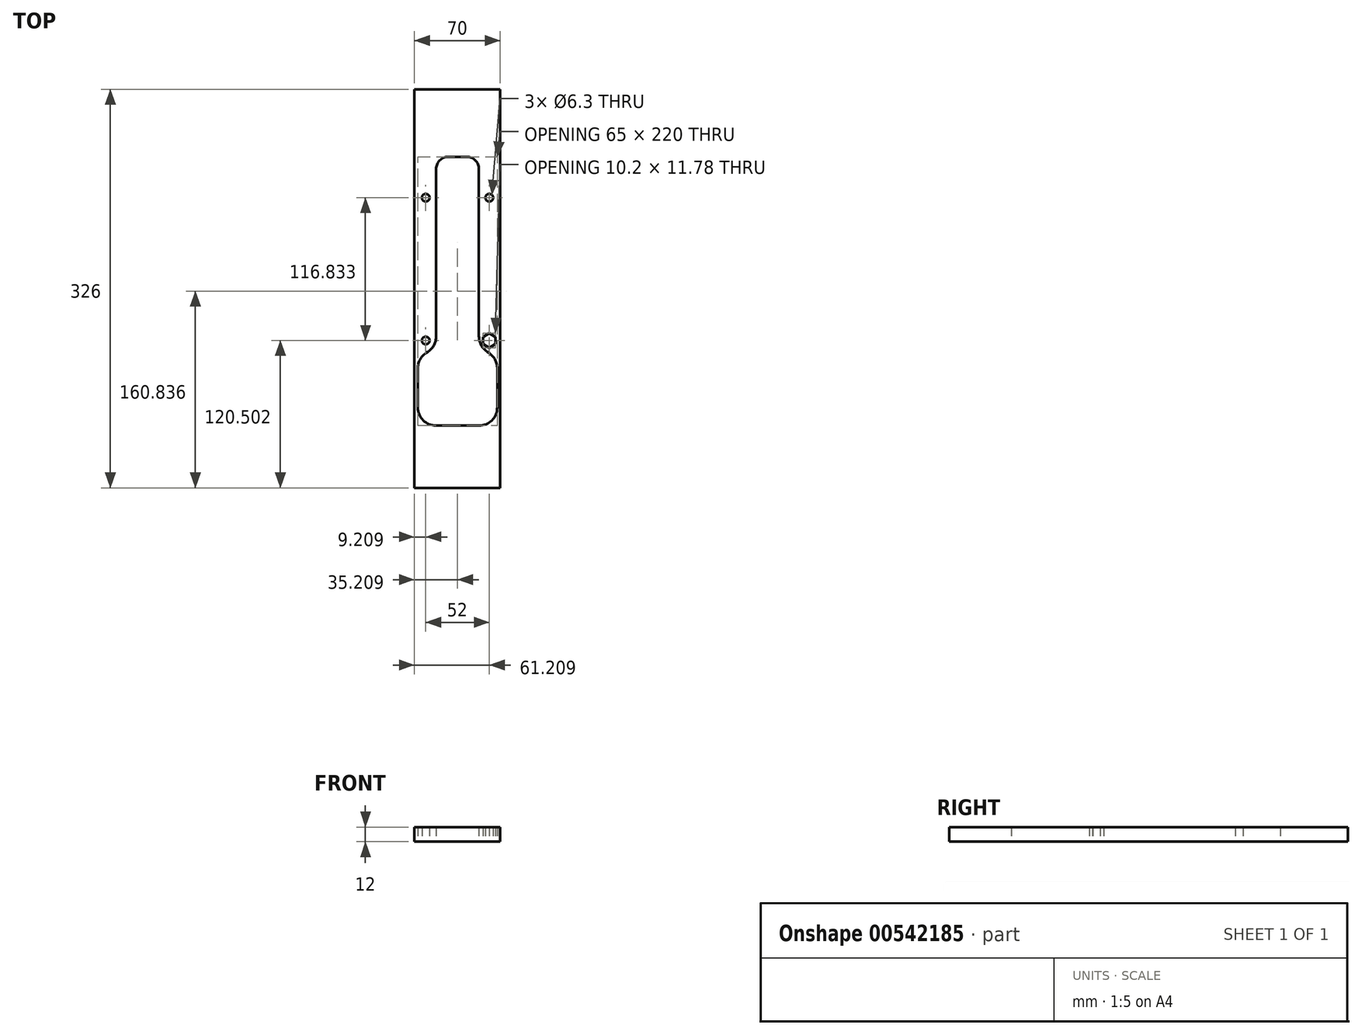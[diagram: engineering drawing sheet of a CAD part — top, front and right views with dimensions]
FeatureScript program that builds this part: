
annotation { "Feature Type Name" : "Feature", "Feature Type Description" : "" }
export const myFeature = defineFeature(function(context is Context, id is Id, definition is map)
    precondition{}
    {
        {
            var Q0;
            Q0=qCreatedBy(makeId("Top.planeOp"),FACE);
            var sketch = newSketch(context, id + "F0", { "sketchPlane" : qUnion([Q0])});
            skLineSegment(sketch, "E0.bottom", {"start": v(17.7, -112.16) * mm, "end": v(-17.3, -112.16) * mm});
            skLineSegment(sketch, "E0.top", {"start": v(17.7, 107.84) * mm, "end": v(-17.3, 107.84) * mm});
            skLineSegment(sketch, "E0.left", {"start": v(17.7, -47.16) * mm, "end": v(17.7, 107.84) * mm});
            skLineSegment(sketch, "E0.right", {"start": v(-17.3, -47.16) * mm, "end": v(-17.3, 107.84) * mm});
            skPoint(sketch, "E0.middle", {"position": v(0.2, -2.16) * mm});
            skLineSegment(sketch, "E1.bottom", {"start": v(32.7, -112.16) * mm, "end": v(-32.3, -112.16) * mm});
            skLineSegment(sketch, "E1.left", {"start": v(32.7, -112.16) * mm, "end": v(32.7, -57.16) * mm});
            skLineSegment(sketch, "E1.right", {"start": v(-32.3, -112.16) * mm, "end": v(-32.3, -57.16) * mm});
            skPoint(sketch, "E1.middle", {"position": v(0.2, -84.66) * mm});
            skPoint(sketch, "E1.middle.positionSnap0", {"position": v(0.2, -112.16) * mm});
            skPoint(sketch, "E1.cornerSnap0", {"position": v(0.2, -112.16) * mm});
            skPoint(sketch, "E1.centerSnap0", {"position": v(0.2, -112.16) * mm});
            skCircle(sketch, "E2", {"center": v(0.2, 94.74) * mm, "radius": 4.1 * mm});
            skCircle(sketch, "E3", {"center": v(-5.8, 82.74) * mm, "radius": 4.1 * mm});
            skCircle(sketch, "E4", {"center": v(6.2, 82.74) * mm, "radius": 4.1 * mm});
            skLineSegment(sketch, "E5", {"start": v(-32.3, -57.16) * mm, "end": v(-17.3, -47.16) * mm});
            skLineSegment(sketch, "E6", {"start": v(17.7, -47.16) * mm, "end": v(32.7, -57.16) * mm});
            skLineSegment(sketch, "E7.0", {"start": v(27.7, -107.16) * mm, "end": v(-27.3, -107.16) * mm});
            skLineSegment(sketch, "E7.1", {"start": v(-27.3, -107.16) * mm, "end": v(-27.3, -59.84) * mm});
            skLineSegment(sketch, "E7.2", {"start": v(27.7, -107.16) * mm, "end": v(27.7, -59.84) * mm});
            skLineSegment(sketch, "E7.3", {"start": v(-27.3, -59.84) * mm, "end": v(-12.3, -49.84) * mm});
            skLineSegment(sketch, "E7.4", {"start": v(12.7, -49.84) * mm, "end": v(27.7, -59.84) * mm});
            skLineSegment(sketch, "E7.5", {"start": v(12.7, -49.84) * mm, "end": v(12.7, 102.84) * mm});
            skLineSegment(sketch, "E7.6", {"start": v(12.7, 102.84) * mm, "end": v(-12.3, 102.84) * mm});
            skLineSegment(sketch, "E7.7", {"start": v(-12.3, -49.84) * mm, "end": v(-12.3, 102.84) * mm});
            skLineSegment(sketch, "E8", {"start": v(-12.3, 61.26) * mm, "end": v(12.7, 61.26) * mm, "construction": true});
            skLineSegment(sketch, "E9", {"start": v(-12.3, -38.74) * mm, "end": v(12.7, -38.74) * mm, "construction": true});
            skCircle(sketch, "E10", {"center": v(0.2, -79.16) * mm, "radius": 5.15 * mm});
            skArc(sketch, "E11", {"start": v(-5.9, -38.74) * mm, "mid": v(0.2, -44.84) * mm, "end": v(6.3, -38.74) * mm});
            skArc(sketch, "E12", {"start": v(-5.9, 61.26) * mm, "mid": v(0.2, 67.36) * mm, "end": v(6.3, 61.26) * mm});
            skLineSegment(sketch, "E13", {"start": v(-5.9, -38.74) * mm, "end": v(-5.9, 61.26) * mm});
            skLineSegment(sketch, "E14", {"start": v(6.3, 61.26) * mm, "end": v(6.3, -38.74) * mm});
            skLineSegment(sketch, "E15", {"start": v(-12.3, -49.84) * mm, "end": v(12.7, -49.84) * mm, "construction": true});
            skLineSegment(sketch, "E16", {"start": v(-32.3, -57.16) * mm, "end": v(-34.3, -47.16) * mm});
            skLineSegment(sketch, "E17", {"start": v(-34.3, -47.16) * mm, "end": v(-34.3, -32.16) * mm});
            skLineSegment(sketch, "E18", {"start": v(-34.3, -32.16) * mm, "end": v(-17.3, -32.16) * mm});
            skCircle(sketch, "E19.cCircle", {"center": v(-25.8, -42.5) * mm, "radius": 5.1 * mm, "construction": true});
            skLineSegment(sketch, "E19.0", {"start": v(-20.7, -39.55) * mm, "end": v(-20.7, -45.44) * mm});
            skLineSegment(sketch, "E19.1", {"start": v(-20.7, -45.44) * mm, "end": v(-25.8, -48.39) * mm});
            skLineSegment(sketch, "E19.2", {"start": v(-25.8, -48.39) * mm, "end": v(-30.9, -45.44) * mm});
            skLineSegment(sketch, "E19.3", {"start": v(-30.9, -45.44) * mm, "end": v(-30.9, -39.55) * mm});
            skLineSegment(sketch, "E19.4", {"start": v(-30.9, -39.55) * mm, "end": v(-25.8, -36.6) * mm});
            skLineSegment(sketch, "E19.5", {"start": v(-25.8, -36.6) * mm, "end": v(-20.7, -39.55) * mm});
            skPoint(sketch, "E19.0.midPoint", {"position": v(-20.7, -42.5) * mm});
            skLineSegment(sketch, "E20", {"start": v(-25.8, -32.16) * mm, "end": v(-25.8, -52.83) * mm, "construction": true});
            skLineSegment(sketch, "E21", {"start": v(-25.8, -42.5) * mm, "end": v(-17.3, -42.5) * mm, "construction": true});
            skCircle(sketch, "E22", {"center": v(-25.8, -42.5) * mm, "radius": 3.15 * mm});
            skLineSegment(sketch, "E23.MirrorCS", {"start": v(26.2, -48.39) * mm, "end": v(31.3, -45.44) * mm});
            skLineSegment(sketch, "E24.MirrorCS", {"start": v(21.1, -39.55) * mm, "end": v(21.1, -45.44) * mm});
            skLineSegment(sketch, "E25.MirrorCS", {"start": v(31.3, -45.44) * mm, "end": v(31.3, -39.55) * mm});
            skLineSegment(sketch, "E26.MirrorCS", {"start": v(31.3, -39.55) * mm, "end": v(26.2, -36.6) * mm});
            skLineSegment(sketch, "E27.MirrorCS", {"start": v(21.1, -45.44) * mm, "end": v(26.2, -48.39) * mm});
            skCircle(sketch, "E28.MirrorC", {"center": v(26.2, -42.5) * mm, "radius": 3.15 * mm});
            skLineSegment(sketch, "E29.MirrorCS", {"start": v(26.2, -36.6) * mm, "end": v(21.1, -39.55) * mm});
            skCircle(sketch, "E30.MirrorC", {"center": v(26.2, -42.5) * mm, "radius": 5.1 * mm, "construction": true});
            skPoint(sketch, "E31.MirrorP", {"position": v(21.1, -42.5) * mm});
            skLineSegment(sketch, "E32.MirrorCS", {"start": v(32.7, -57.16) * mm, "end": v(34.7, -47.16) * mm});
            skLineSegment(sketch, "E33.MirrorCS", {"start": v(34.7, -47.16) * mm, "end": v(34.7, -32.16) * mm});
            skLineSegment(sketch, "E34.MirrorCS", {"start": v(34.7, -32.16) * mm, "end": v(17.7, -32.16) * mm});
            skPoint(sketch, "E35.visualSharp", {"position": v(-34.3, -32.16) * mm});
            skLineSegment(sketch, "E35.filletArc", {"start": v(-34.3, -32.16) * mm, "end": v(-34.3, -32.16) * mm});
            skPoint(sketch, "E36.visualSharp", {"position": v(34.7, -32.16) * mm});
            skLineSegment(sketch, "E36.filletArc", {"start": v(34.7, -32.16) * mm, "end": v(34.7, -32.16) * mm});
            skLineSegment(sketch, "E37", {"start": v(-17.3, 82.84) * mm, "end": v(-34.3, 82.84) * mm});
            skLineSegment(sketch, "E38", {"start": v(-34.3, 82.84) * mm, "end": v(-34.3, 65.84) * mm});
            skLineSegment(sketch, "E39", {"start": v(-34.3, 65.84) * mm, "end": v(-17.3, 65.84) * mm});
            skCircle(sketch, "E40.cCircle", {"center": v(-25.8, 74.34) * mm, "radius": 5.1 * mm, "construction": true});
            skPoint(sketch, "E40.cCircle.centerSnap0", {"position": v(-25.8, 65.84) * mm});
            skPoint(sketch, "E40.cCircle.centerSnap1", {"position": v(-34.3, 74.34) * mm});
            skLineSegment(sketch, "E40.0", {"start": v(-20.7, 71.4) * mm, "end": v(-25.8, 68.45) * mm});
            skLineSegment(sketch, "E40.1", {"start": v(-25.8, 68.45) * mm, "end": v(-30.9, 71.4) * mm});
            skLineSegment(sketch, "E40.2", {"start": v(-30.9, 71.4) * mm, "end": v(-30.9, 77.28) * mm});
            skLineSegment(sketch, "E40.3", {"start": v(-30.9, 77.28) * mm, "end": v(-25.8, 80.22) * mm});
            skLineSegment(sketch, "E40.4", {"start": v(-25.8, 80.22) * mm, "end": v(-20.7, 77.28) * mm});
            skLineSegment(sketch, "E40.5", {"start": v(-20.7, 77.28) * mm, "end": v(-20.7, 71.4) * mm});
            skPoint(sketch, "E40.0.midPoint", {"position": v(-23.24, 69.92) * mm});
            skCircle(sketch, "E41", {"center": v(-25.8, 74.34) * mm, "radius": 3.15 * mm});
            skLineSegment(sketch, "E42.MirrorCS", {"start": v(26.2, 68.45) * mm, "end": v(31.3, 71.4) * mm});
            skLineSegment(sketch, "E43.MirrorCS", {"start": v(31.3, 71.4) * mm, "end": v(31.3, 77.28) * mm});
            skLineSegment(sketch, "E44.MirrorCS", {"start": v(21.1, 71.4) * mm, "end": v(26.2, 68.45) * mm});
            skLineSegment(sketch, "E45.MirrorCS", {"start": v(31.3, 77.28) * mm, "end": v(26.2, 80.22) * mm});
            skLineSegment(sketch, "E46.MirrorCS", {"start": v(34.7, 82.84) * mm, "end": v(34.7, 65.84) * mm});
            skPoint(sketch, "E47.MirrorP", {"position": v(26.2, 65.84) * mm});
            skPoint(sketch, "E48.MirrorP", {"position": v(34.7, 74.34) * mm});
            skLineSegment(sketch, "E49.MirrorCS", {"start": v(21.1, 77.28) * mm, "end": v(21.1, 71.4) * mm});
            skLineSegment(sketch, "E50.MirrorCS", {"start": v(26.2, 80.22) * mm, "end": v(21.1, 77.28) * mm});
            skCircle(sketch, "E51.MirrorC", {"center": v(26.2, 74.34) * mm, "radius": 5.1 * mm, "construction": true});
            skPoint(sketch, "E52.MirrorP", {"position": v(23.66, 69.92) * mm});
            skCircle(sketch, "E53.MirrorC", {"center": v(26.2, 74.34) * mm, "radius": 3.15 * mm});
            skLineSegment(sketch, "E54.MirrorCS", {"start": v(34.7, 65.84) * mm, "end": v(17.7, 65.84) * mm});
            skLineSegment(sketch, "E55.MirrorCS", {"start": v(17.7, 82.84) * mm, "end": v(34.7, 82.84) * mm});
            skLineSegment(sketch, "E56.bottom", {"start": v(35, -163) * mm, "end": v(-35, -163) * mm});
            skLineSegment(sketch, "E56.top", {"start": v(35, 163) * mm, "end": v(-35, 163) * mm});
            skLineSegment(sketch, "E56.left", {"start": v(35, -163) * mm, "end": v(35, 163) * mm});
            skLineSegment(sketch, "E56.right", {"start": v(-35, -163) * mm, "end": v(-35, 163) * mm});
            skPoint(sketch, "E56.middle", {"position": v(0, 0) * mm});
            skSolve(sketch);
        }
        {
            var Q0;
            {var subQ6=sQuery(id+"F0.wireOp",EDGE,"E0.top");Q0=makeQuery(id+"F0.imprint","IMPRINT",FACE,{"disambiguationData":[TD([[makeQuery(id+"F0.imprint","IMPRINT",EDGE,{"derivedFrom":subQ6}),-1.0]])]});}
            var Q1;
            {var subQ1=sQuery(id+"F0.wireOp",EDGE,"E5");Q1=makeQuery(id+"F0.imprint","IMPRINT",FACE,{"disambiguationData":[TD([[makeQuery(id+"F0.imprint","IMPRINT",EDGE,{"derivedFrom":subQ1}),1.0]])]});}
            var Q2;
            Q2=makeQuery(id+"F0.imprint","IMPRINT",FACE,{"disambiguationData":[TD([[makeQuery(id+"F0.imprint","IMPRINT",EDGE,{"derivedFrom":sQuery(id+"F0.wireOp",EDGE,"E19.0")}),-1.0]])]});
            var Q3;
            Q3=makeQuery(id+"F0.imprint","IMPRINT",FACE,{"disambiguationData":[TD([[makeQuery(id+"F0.imprint","IMPRINT",EDGE,{"derivedFrom":sQuery(id+"F0.wireOp",EDGE,"E23.MirrorCS")}),1.0]])]});
            var Q4;
            {var subQ0=sQuery(id+"F0.wireOp",EDGE,"E6");Q4=makeQuery(id+"F0.imprint","IMPRINT",FACE,{"disambiguationData":[TD([[makeQuery(id+"F0.imprint","IMPRINT",EDGE,{"derivedFrom":subQ0}),1.0]])]});}
            var Q5;
            {var subQ1=sQuery(id+"F0.wireOp",EDGE,"E37");Q5=makeQuery(id+"F0.imprint","IMPRINT",FACE,{"disambiguationData":[TD([[makeQuery(id+"F0.imprint","IMPRINT",EDGE,{"derivedFrom":subQ1}),1.0]])]});}
            var Q6;
            Q6=makeQuery(id+"F0.imprint","IMPRINT",FACE,{"disambiguationData":[TD([[makeQuery(id+"F0.imprint","IMPRINT",EDGE,{"derivedFrom":sQuery(id+"F0.wireOp",EDGE,"E42.MirrorCS")}),-1.0]])]});
            var Q7;
            Q7=makeQuery(id+"F0.imprint","IMPRINT",FACE,{"disambiguationData":[TD([[makeQuery(id+"F0.imprint","IMPRINT",EDGE,{"derivedFrom":sQuery(id+"F0.wireOp",EDGE,"E40.0")}),-1.0]])]});
            var Q8;
            Q8=makeQuery(id+"F0.imprint","IMPRINT",FACE,{"disambiguationData":[TD([[makeQuery(id+"F0.imprint","IMPRINT",EDGE,{"derivedFrom":sQuery(id+"F0.wireOp",EDGE,"E42.MirrorCS")}),1.0]])]});
            extrude(context, id + "F1", {"entities" : qUnion([Q0, Q1, Q2, Q3, Q4, Q5, Q6, Q7, Q8]), "depth" : 12 * mm, "offsetDistance" : 25 * mm});
        }
        {
            var Q0;
            Q0=makeQuery(id+"F1.opExtrude","SWEPT_EDGE",EDGE,{"disambiguationData":[OSD([sQuery(id+"F0.wireOp",EDGE,"E1.right"),sQuery(id+"F0.wireOp",EDGE,"E5"),sQuery(id+"F0.wireOp",EDGE,"E16")])]});
            var Q1;
            Q1=makeQuery(id+"F1.opExtrude","SWEPT_EDGE",EDGE,{"disambiguationData":[OSD([sQuery(id+"F0.wireOp",EDGE,"E0.right"),sQuery(id+"F0.wireOp",EDGE,"E5")])]});
            var Q2;
            Q2=makeQuery(id+"F1.opExtrude","SWEPT_EDGE",EDGE,{"disambiguationData":[OSD([sQuery(id+"F0.wireOp",EDGE,"E0.left"),sQuery(id+"F0.wireOp",EDGE,"E6")])]});
            var Q3;
            Q3=makeQuery(id+"F1.opExtrude","SWEPT_EDGE",EDGE,{"disambiguationData":[OSD([sQuery(id+"F0.wireOp",EDGE,"E1.left"),sQuery(id+"F0.wireOp",EDGE,"E6"),sQuery(id+"F0.wireOp",EDGE,"E32.MirrorCS")])]});
            var Q4;
            Q4=makeQuery(id+"F1.opExtrude","SWEPT_EDGE",EDGE,{"disambiguationData":[OSD([sQuery(id+"F0.wireOp",EDGE,"E1.bottom"),sQuery(id+"F0.wireOp",EDGE,"E1.left")])]});
            var Q5;
            Q5=makeQuery(id+"F1.opExtrude","SWEPT_EDGE",EDGE,{"disambiguationData":[OSD([sQuery(id+"F0.wireOp",EDGE,"E1.bottom"),sQuery(id+"F0.wireOp",EDGE,"E1.right")])]});
            fillet(context, id + "F2", {"entities" : qUnion([Q0, Q1, Q2, Q3, Q4, Q5]), "radius" : 15 * mm, "tangentPropagation" : true, "allowEdgeOverflow" : false});
        }
        {
            var Q0;
            Q0=makeQuery(id+"F1.opExtrude","SWEPT_EDGE",EDGE,{"disambiguationData":[OSD([sQuery(id+"F0.wireOp",EDGE,"E0.top"),sQuery(id+"F0.wireOp",EDGE,"E0.left")])]});
            var Q1;
            Q1=makeQuery(id+"F1.opExtrude","SWEPT_EDGE",EDGE,{"disambiguationData":[OSD([sQuery(id+"F0.wireOp",EDGE,"E0.top"),sQuery(id+"F0.wireOp",EDGE,"E0.right")])]});
            fillet(context, id + "F3", {"entities" : qUnion([Q0, Q1]), "radius" : 10 * mm, "tangentPropagation" : true, "allowEdgeOverflow" : false});
        }
    });
